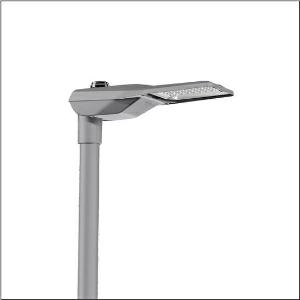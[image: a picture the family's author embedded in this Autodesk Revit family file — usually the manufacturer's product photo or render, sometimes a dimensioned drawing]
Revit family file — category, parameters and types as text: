
# Revit family: streetlight_sl_21_mini___st1_0a_5xe6d57n08jb_a4a3
name_source: partatom
category: Lighting Fixtures
units: mm (PartAtom-declared; Revit-internal decimal feet)

## family parameters
Cut with Voids When Loaded = No
Host = Face
Light Source = No
Part Type = Normal
Room Calculation Point = No
Round Connector Dimension = Use Diameter
Shared = No

## types (1)
- --- (1 x LED, 11030 lm, 87.3 W, 3000K)
    Apparent Load = 87 VA
    CIE Flux Codes = 40 73 97 100 100
    Color Rendering = 80
    Color Temperature = 3000K
    Default Elevation = 1800 mm
    Description = Streetlight SL 21 mini, mast luminaire, primary light control with lens, of PMMA, primary optical cover: cover, of toughened safety glass, transparent, light distribution: ST1.0a, light emission: direct distribution, primary light characteristic: asymmetric, installation type: side-entry, LED, 3G 2.5mm², High Power LED, rated luminous flux: 11.030lm, luminous efficacy: 126lm/W, light colour: 830, colour temperature: 3000K, control: overheat protection, pre-setting: linear dimming characteristic, constant luminous flux control, time-dependent luminous flux control, flexible luminous flux parameterisation, mains connection: 230..240V, AC, 50/60Hz, connection cable pre-assembled, cable length: 10,5m, wiring characteristics: H05VV-F, start of lifetime: 87W, end of service life: 90W, reduction: 40W, luminaire housing, of diecast aluminium (EN AC-44300), powder-coated, Siteco® metallic grey (DB 702S), corrosivity category C5 mid according to DIN EN ISO 12944, multi-level sealing system, sealing non-destructively replaceable, inclination adjustable: 0°, 5°, 10°, 15°, length: 628mm, width: 235mm, height: 110mm, spigot size: 42mm (side-entry), protection rating (complete): IP66, insulation class (complete): insulation class I (protective earthing), certification: CE, ENEC, ENEC+, VDE, impact resistance: IK09, permissible operating ambient temperature for outdoor applications: -40..+50°C, standard-compliant lighting for roads and squares, packaging unit: 1 piece

Light Distribution: ST1.0a
    Height = 110 mm
    Lamp = 1 x LED
    Lamp Light Flux = 11030 lm
    Lamp Power = 87.3 W
    Lamp count = 1
    Length = 625 mm
    Luminous efficacy = 126 lm/W
    Manufacturer = Siteco
    ModVariant = No
    Model = 5XE6D57N08JB
    Number of Poles = 1
    OnlyDefault = Yes
    Power Factor = 1
    Product Name = Streetlight SL 21 mini | ST1.0a
    Product group = mast luminaire | pylon top
    ProductGroupID = 6100
    Protection Class = Protection class I
    Protection Degree = IP 66
    RLX_Detail_Level = 1
    RLX_Emergency_Light_Flux = 0 lm
    RLX_Emergency_Type = 0
    RLX_Emergency_Type_DB = No
    RlxData = <blob elided: 91741 chars, md5=4001aea1>
    Socket = socket
    Standby Power = 0 W
    System Light Flux = 11030 lm
    System Power = 87 W
    Type Comments = factory setting: luminous flux: 100 % | dim-lin: 254 | 915 mA
    Type Image = l_1294379.jpg
    URL = http://relux.com
    VarID = @adj_105085
    Voltage = 0 V
    Weight = 0.00 kg
    Width = 234 mm

## geometry (parser evidence)
native form markers: Blend x4, Sweep x10
no freeform markers — native parametric forms only
